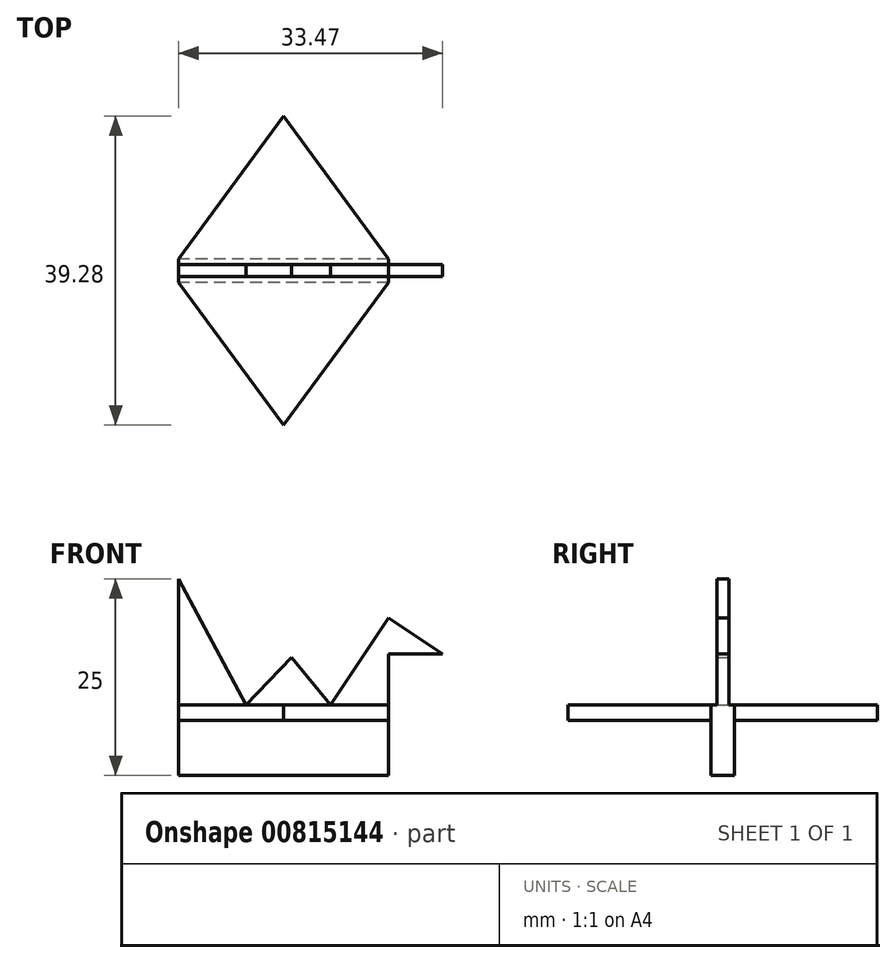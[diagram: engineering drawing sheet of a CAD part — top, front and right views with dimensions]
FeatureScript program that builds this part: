
annotation { "Feature Type Name" : "Feature", "Feature Type Description" : "" }
export const myFeature = defineFeature(function(context is Context, id is Id, definition is map)
    precondition{}
    {
        {
            var Q0;
            Q0=qCreatedBy(makeId("Front.planeOp"),FACE);
            var sketch = newSketch(context, id + "F0", { "sketchPlane" : qUnion([Q0])});
            skLineSegment(sketch, "E0", {"start": v(0, 0) * mm, "end": v(-13.33, 25) * mm});
            skLineSegment(sketch, "E1", {"start": v(-13.33, 25) * mm, "end": v(-13.33, 0) * mm});
            skLineSegment(sketch, "E2", {"start": v(-13.33, 0) * mm, "end": v(0, 0) * mm});
            skLineSegment(sketch, "E3", {"start": v(0, 0) * mm, "end": v(13.33, 20) * mm});
            skLineSegment(sketch, "E4", {"start": v(13.33, 20) * mm, "end": v(13.33, 0) * mm});
            skLineSegment(sketch, "E5", {"start": v(13.33, 0) * mm, "end": v(0, 0) * mm});
            skLineSegment(sketch, "E6", {"start": v(13.33, 20) * mm, "end": v(20.14, 15.46) * mm});
            skLineSegment(sketch, "E7", {"start": v(20.14, 15.46) * mm, "end": v(13.33, 15.46) * mm});
            skLineSegment(sketch, "E8", {"start": v(-13.33, 0) * mm, "end": v(1, 15) * mm});
            skLineSegment(sketch, "E9", {"start": v(1, 15) * mm, "end": v(13.33, 0) * mm});
            skLineSegment(sketch, "E10", {"start": v(-13.33, 8.95) * mm, "end": v(13.33, 8.95) * mm});
            skPoint(sketch, "E11", {"position": v(-4.77, 8.95) * mm});
            skPoint(sketch, "E12", {"position": v(5.97, 8.95) * mm});
            skSolve(sketch);
        }
        {
            var Q0;
            {var subQ0=sQuery(id+"F0.wireOp",EDGE,"E1");Q0=makeQuery(id+"F0.imprint","IMPRINT",FACE,{"disambiguationData":[TD([[makeQuery(id+"F0.imprint","IMPRINT",EDGE,{"derivedFrom":subQ0}),1.0]])]});}
            var Q1;
            {var subQ0=sQuery(id+"F0.wireOp",EDGE,"E2");Q1=makeQuery(id+"F0.imprint","IMPRINT",FACE,{"disambiguationData":[TD([[makeQuery(id+"F0.imprint","IMPRINT",EDGE,{"derivedFrom":subQ0}),1.0]])]});}
            var Q2;
            {var subQ3=sQuery(id+"F0.wireOp",EDGE,"E8");var subQ5=sQuery(id+"F0.wireOp",EDGE,"E9");var subQ7=makeQuery(id+"F0.imprint","INTERSECT",VERTEX,{"derivedFrom":[subQ3,subQ5]});Q2=makeQuery(id+"F0.imprint","IMPRINT",FACE,{"disambiguationData":[TD([[makeQuery(id+"F0.imprint","IMPRINT",EDGE,{"disambiguationData":[TD([[subQ7,1.0]])],"derivedFrom":subQ3}),-1.0]])]});}
            var Q3;
            {var subQ0=sQuery(id+"F0.wireOp",EDGE,"E5");Q3=makeQuery(id+"F0.imprint","IMPRINT",FACE,{"disambiguationData":[TD([[makeQuery(id+"F0.imprint","IMPRINT",EDGE,{"derivedFrom":subQ0}),-1.0]])]});}
            var Q4;
            {var subQ1=sQuery(id+"F0.wireOp",EDGE,"E3");var subQ3=sQuery(id+"F0.wireOp",EDGE,"E9");var subQ4=makeQuery(id+"F0.imprint","INTERSECT",VERTEX,{"derivedFrom":[subQ1,subQ3]});Q4=makeQuery(id+"F0.imprint","IMPRINT",FACE,{"disambiguationData":[TD([[makeQuery(id+"F0.imprint","IMPRINT",EDGE,{"disambiguationData":[TD([[subQ4,-1.0]])],"derivedFrom":subQ1}),-1.0]])]});}
            var Q5;
            {var subQ0=sQuery(id+"F0.wireOp",EDGE,"E6");Q5=makeQuery(id+"F0.imprint","IMPRINT",FACE,{"disambiguationData":[TD([[makeQuery(id+"F0.imprint","IMPRINT",EDGE,{"derivedFrom":subQ0}),-1.0]])]});}
            var Q6;
            {var subQ1=sQuery(id+"F0.wireOp",EDGE,"E0");var subQ3=sQuery(id+"F0.wireOp",EDGE,"E10");var subQ4=makeQuery(id+"F0.imprint","INTERSECT",VERTEX,{"derivedFrom":[subQ1,sQuery(id+"F0.wireOp",EDGE,"E8"),subQ3]});Q6=makeQuery(id+"F0.imprint","IMPRINT",FACE,{"disambiguationData":[TD([[makeQuery(id+"F0.imprint","IMPRINT",EDGE,{"disambiguationData":[TD([[subQ4,-1.0]])],"derivedFrom":subQ3}),-1.0]])]});}
            var Q7;
            {var subQ1=sQuery(id+"F0.wireOp",EDGE,"E4");var subQ3=sQuery(id+"F0.wireOp",EDGE,"E10");var subQ4=makeQuery(id+"F0.imprint","INTERSECT",VERTEX,{"derivedFrom":[subQ1,subQ3]});Q7=makeQuery(id+"F0.imprint","IMPRINT",FACE,{"disambiguationData":[TD([[makeQuery(id+"F0.imprint","IMPRINT",EDGE,{"disambiguationData":[TD([[subQ4,-1.0]])],"derivedFrom":subQ1}),-1.0]])]});}
            extrude(context, id + "F1", {"entities" : qUnion([Q0, Q1, Q2, Q3, Q4, Q5, Q6, Q7]), "endBound" : BoundingType.SYMMETRIC, "depth" : 1.5 * mm, "offsetDistance" : 25 * mm});
        }
        {
            var Q0;
            {var subQ1=sQuery(id+"F0.wireOp",EDGE,"E1");var subQ3=sQuery(id+"F0.wireOp",EDGE,"E10");var subQ4=makeQuery(id+"F0.imprint","INTERSECT",VERTEX,{"derivedFrom":[subQ1,subQ3]});Q0=makeQuery(id+"F0.imprint","IMPRINT",FACE,{"disambiguationData":[TD([[makeQuery(id+"F0.imprint","IMPRINT",EDGE,{"disambiguationData":[TD([[subQ4,-1.0]])],"derivedFrom":subQ1}),1.0]])]});}
            var Q1;
            {var subQ0=sQuery(id+"F0.wireOp",EDGE,"E2");Q1=makeQuery(id+"F0.imprint","IMPRINT",FACE,{"disambiguationData":[TD([[makeQuery(id+"F0.imprint","IMPRINT",EDGE,{"derivedFrom":subQ0}),1.0]])]});}
            var Q2;
            {var subQ1=sQuery(id+"F0.wireOp",EDGE,"E0");var subQ3=sQuery(id+"F0.wireOp",EDGE,"E10");var subQ4=makeQuery(id+"F0.imprint","INTERSECT",VERTEX,{"derivedFrom":[subQ1,sQuery(id+"F0.wireOp",EDGE,"E8"),subQ3]});Q2=makeQuery(id+"F0.imprint","IMPRINT",FACE,{"disambiguationData":[TD([[makeQuery(id+"F0.imprint","IMPRINT",EDGE,{"disambiguationData":[TD([[subQ4,-1.0]])],"derivedFrom":subQ3}),-1.0]])]});}
            var Q3;
            {var subQ0=sQuery(id+"F0.wireOp",EDGE,"E5");Q3=makeQuery(id+"F0.imprint","IMPRINT",FACE,{"disambiguationData":[TD([[makeQuery(id+"F0.imprint","IMPRINT",EDGE,{"derivedFrom":subQ0}),-1.0]])]});}
            var Q4;
            {var subQ1=sQuery(id+"F0.wireOp",EDGE,"E4");var subQ3=sQuery(id+"F0.wireOp",EDGE,"E10");var subQ4=makeQuery(id+"F0.imprint","INTERSECT",VERTEX,{"derivedFrom":[subQ1,subQ3]});Q4=makeQuery(id+"F0.imprint","IMPRINT",FACE,{"disambiguationData":[TD([[makeQuery(id+"F0.imprint","IMPRINT",EDGE,{"disambiguationData":[TD([[subQ4,-1.0]])],"derivedFrom":subQ1}),-1.0]])]});}
            extrude(context, id + "F2", {"entities" : qUnion([Q0, Q1, Q2, Q3, Q4]), "operationType" : NewBodyOperationType.ADD, "endBound" : BoundingType.SYMMETRIC, "depth" : 3 * mm, "offsetDistance" : 25 * mm});
        }
        {
            var Q0;
            Q0=qCreatedBy(makeId("Top.planeOp"),FACE);
            var sketch = newSketch(context, id + "F3", { "sketchPlane" : qUnion([Q0])});
            skPoint(sketch, "E13.0", {"position": v(-13.33, 0) * mm});
            skPoint(sketch, "E14.0", {"position": v(13.33, 0) * mm});
            skLineSegment(sketch, "E15.0", {"start": v(-13.33, -0.75) * mm, "end": v(-13.33, 0.75) * mm});
            skLineSegment(sketch, "E16.0", {"start": v(-4.77, 0.75) * mm, "end": v(-13.33, 0.75) * mm});
            skLineSegment(sketch, "E17.0", {"start": v(-4.77, -0.75) * mm, "end": v(-13.33, -0.75) * mm});
            skLineSegment(sketch, "E18.0.0", {"start": v(13.33, 0.75) * mm, "end": v(5.97, 0.75) * mm});
            skLineSegment(sketch, "E18.0.1", {"start": v(5.97, 0.75) * mm, "end": v(5.97, -0.75) * mm});
            skLineSegment(sketch, "E18.0.2", {"start": v(5.97, -0.75) * mm, "end": v(13.33, -0.75) * mm});
            skLineSegment(sketch, "E18.0.3", {"start": v(13.33, -0.75) * mm, "end": v(13.33, 0.75) * mm});
            skLineSegment(sketch, "E19.0.0", {"start": v(5.97, 0.75) * mm, "end": v(13.33, 0.75) * mm});
            skLineSegment(sketch, "E19.0.1", {"start": v(13.33, 0.75) * mm, "end": v(13.33, 1.5) * mm});
            skLineSegment(sketch, "E19.0.2", {"start": v(13.33, 1.5) * mm, "end": v(-13.33, 1.5) * mm});
            skLineSegment(sketch, "E19.0.3", {"start": v(-13.33, 1.5) * mm, "end": v(-13.33, 0.75) * mm});
            skLineSegment(sketch, "E19.0.4", {"start": v(-13.33, 0.75) * mm, "end": v(-4.77, 0.75) * mm});
            skLineSegment(sketch, "E19.0.5", {"start": v(-4.77, 0.75) * mm, "end": v(5.97, 0.75) * mm});
            skLineSegment(sketch, "E20.0", {"start": v(-13.33, -1.5) * mm, "end": v(13.33, -1.5) * mm});
            skLineSegment(sketch, "E21", {"start": v(-13.33, 1.5) * mm, "end": v(0, 19.64) * mm});
            skLineSegment(sketch, "E22", {"start": v(0, 19.64) * mm, "end": v(13.33, 1.5) * mm});
            skLineSegment(sketch, "E23", {"start": v(-13.33, -1.5) * mm, "end": v(0, -19.64) * mm});
            skLineSegment(sketch, "E24", {"start": v(0, -19.64) * mm, "end": v(13.33, -1.5) * mm});
            skLineSegment(sketch, "E25", {"start": v(-13.33, -1.5) * mm, "end": v(-13.33, -0.75) * mm});
            skLineSegment(sketch, "E26", {"start": v(13.33, -1.5) * mm, "end": v(13.33, -0.75) * mm});
            skSolve(sketch);
        }
        {
            var Q0;
            Q0=makeQuery(id+"F3.imprint","IMPRINT",FACE,{"disambiguationData":[TD([[makeQuery(id+"F3.imprint","IMPRINT",EDGE,{"derivedFrom":sQuery(id+"F3.wireOp",EDGE,"E19.0.2")}),-1.0]])]});
            var Q1;
            Q1=makeQuery(id+"F3.imprint","IMPRINT",FACE,{"disambiguationData":[TD([[makeQuery(id+"F3.imprint","IMPRINT",EDGE,{"derivedFrom":sQuery(id+"F3.wireOp",EDGE,"E19.0.0")}),1.0]])]});
            var Q2;
            Q2=makeQuery(id+"F3.imprint","IMPRINT",FACE,{"disambiguationData":[TD([[makeQuery(id+"F3.imprint","IMPRINT",EDGE,{"derivedFrom":sQuery(id+"F3.wireOp",EDGE,"E18.0.1")}),1.0]])]});
            var Q3;
            Q3=makeQuery(id+"F3.imprint","IMPRINT",FACE,{"disambiguationData":[TD([[makeQuery(id+"F3.imprint","IMPRINT",EDGE,{"derivedFrom":sQuery(id+"F3.wireOp",EDGE,"E20.0")}),-1.0]])]});
            var Q4;
            Q4=makeQuery(id+"F3.imprint","IMPRINT",FACE,{"disambiguationData":[TD([[makeQuery(id+"F3.imprint","IMPRINT",EDGE,{"derivedFrom":sQuery(id+"F3.wireOp",EDGE,"E15.0")}),-1.0]])]});
            extrude(context, id + "F4", {"entities" : qUnion([Q0, Q1, Q2, Q3, Q4]), "operationType" : NewBodyOperationType.ADD, "depth" : 8.95 * mm, "offsetDistance" : 25 * mm, "hasSecondDirection" : true, "secondDirectionOppositeDirection" : false, "secondDirectionDepth" : 7 * mm});
        }
    });
